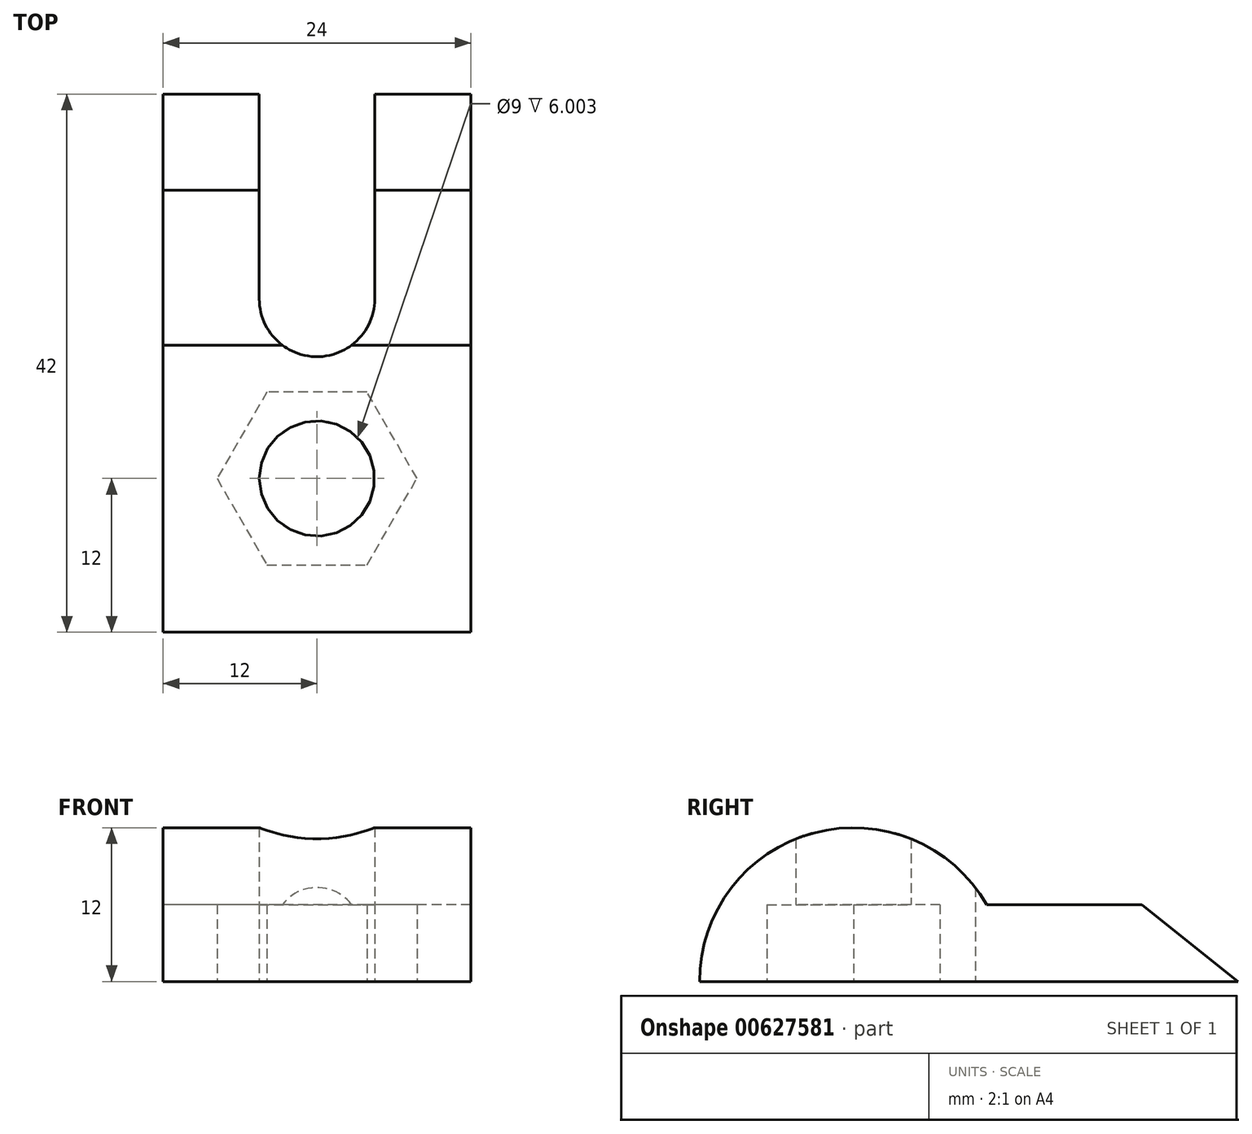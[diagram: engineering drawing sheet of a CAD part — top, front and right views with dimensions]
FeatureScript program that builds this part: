
annotation { "Feature Type Name" : "Feature", "Feature Type Description" : "" }
export const myFeature = defineFeature(function(context is Context, id is Id, definition is map)
    precondition{}
    {
        {
            var Q0;
            Q0=qCreatedBy(makeId("Right.planeOp"),FACE);
            var sketch = newSketch(context, id + "F0", { "sketchPlane" : qUnion([Q0])});
            skArc(sketch, "E0", {"start": v(10.4, 6) * mm, "mid": v(-3.1, 11.6) * mm, "end": v(-12, 0) * mm});
            skLineSegment(sketch, "E1", {"start": v(0, 0) * mm, "end": v(30, 0) * mm});
            skLineSegment(sketch, "E2", {"start": v(10.4, 6) * mm, "end": v(22.5, 6) * mm});
            skLineSegment(sketch, "E3", {"start": v(22.5, 6) * mm, "end": v(30, 0) * mm});
            skLineSegment(sketch, "E4", {"start": v(0, 0) * mm, "end": v(-12, 0) * mm});
            skSolve(sketch);
        }
        {
            var Q0;
            Q0=makeQuery(id+"F0.imprint","IMPRINT",FACE,{"disambiguationData":[TD([[makeQuery(id+"F0.imprint","IMPRINT",EDGE,{"derivedFrom":sQuery(id+"F0.wireOp",EDGE,"E0")}),1.0]])]});
            extrude(context, id + "F1", {"entities" : qUnion([Q0]), "depth" : 24 * mm, "offsetDistance" : 25 * mm});
        }
        {
            var Q0;
            Q0=makeQuery(id+"F1.opExtrude","SWEPT_FACE",FACE,{"disambiguationData":[OSD([sQuery(id+"F0.wireOp",EDGE,"E1"),sQuery(id+"F0.wireOp",EDGE,"E4")])]});
            var sketch = newSketch(context, id + "F2", { "sketchPlane" : qUnion([Q0])});
            skLineSegment(sketch, "E5", {"start": v(24, -30) * mm, "end": v(16.5, -30) * mm});
            skLineSegment(sketch, "E6", {"start": v(16.5, -30) * mm, "end": v(7.5, -30) * mm});
            skLineSegment(sketch, "E7", {"start": v(7.5, -30) * mm, "end": v(0, -30) * mm});
            skLineSegment(sketch, "E8", {"start": v(7.5, -30) * mm, "end": v(7.5, -14) * mm});
            skLineSegment(sketch, "E9", {"start": v(16.5, -30) * mm, "end": v(16.5, -14) * mm});
            skLineSegment(sketch, "E10", {"start": v(16.5, -14) * mm, "end": v(12, -14) * mm});
            skArc(sketch, "E11", {"start": v(16.5, -14) * mm, "mid": v(12, -9.5) * mm, "end": v(7.5, -14) * mm});
            skLineSegment(sketch, "E12", {"start": v(0, 0) * mm, "end": v(12, 0) * mm});
            skCircle(sketch, "E13", {"center": v(12, 0) * mm, "radius": 4.5 * mm});
            skLineSegment(sketch, "E14", {"start": v(12, 0) * mm, "end": v(12, -6.75) * mm});
            skCircle(sketch, "E15.cCircle", {"center": v(12, 0) * mm, "radius": 6.75 * mm, "construction": true});
            skLineSegment(sketch, "E15.0", {"start": v(15.9, -6.75) * mm, "end": v(8.1, -6.75) * mm});
            skLineSegment(sketch, "E15.1", {"start": v(8.1, -6.75) * mm, "end": v(4.2, 0) * mm});
            skLineSegment(sketch, "E15.2", {"start": v(4.2, 0) * mm, "end": v(8.1, 6.75) * mm});
            skLineSegment(sketch, "E15.3", {"start": v(8.1, 6.75) * mm, "end": v(15.9, 6.75) * mm});
            skLineSegment(sketch, "E15.4", {"start": v(15.9, 6.75) * mm, "end": v(19.8, 0) * mm});
            skLineSegment(sketch, "E15.5", {"start": v(19.8, 0) * mm, "end": v(15.9, -6.75) * mm});
            skPoint(sketch, "E15.0.midPoint", {"position": v(12, -6.75) * mm});
            skSolve(sketch);
        }
        {
            var Q0;
            Q0=makeQuery(id+"F2.imprint","IMPRINT",FACE,{"disambiguationData":[TD([[makeQuery(id+"F2.imprint","IMPRINT",EDGE,{"derivedFrom":sQuery(id+"F2.wireOp",EDGE,"E6")}),-1.0]])]});
            var Q1;
            Q1=makeQuery(id+"F2.imprint","IMPRINT",FACE,{"disambiguationData":[TD([[makeQuery(id+"F2.imprint","IMPRINT",EDGE,{"derivedFrom":sQuery(id+"F2.wireOp",EDGE,"E13")}),1.0]])]});
            extrude(context, id + "F3", {"entities" : qUnion([Q0, Q1]), "operationType" : NewBodyOperationType.REMOVE, "oppositeDirection" : true, "depth" : 25 * mm, "offsetDistance" : 25 * mm});
        }
        {
            var Q0;
            {var subQ8=sQuery(id+"F2.wireOp",EDGE,"E15.2");Q0=makeQuery(id+"F2.imprint","IMPRINT",FACE,{"disambiguationData":[TD([[makeQuery(id+"F2.imprint","IMPRINT",EDGE,{"derivedFrom":subQ8}),-1.0]])]});}
            var Q1;
            {var subQ3=sQuery(id+"F2.wireOp",EDGE,"E15.1");Q1=makeQuery(id+"F2.imprint","IMPRINT",FACE,{"disambiguationData":[TD([[makeQuery(id+"F2.imprint","IMPRINT",EDGE,{"derivedFrom":subQ3}),-1.0]])]});}
            extrude(context, id + "F4", {"entities" : qUnion([Q0, Q1]), "operationType" : NewBodyOperationType.REMOVE, "oppositeDirection" : true, "depth" : 6 * mm, "offsetDistance" : 25 * mm});
        }
        {
            var Q0;
            Q0=makeQuery(id+"F1.opExtrude","CAP_FACE",FACE,{"disambiguationData":[OSD([sQuery(id+"F0.wireOp",EDGE,"E0"),sQuery(id+"F0.wireOp",EDGE,"E1"),sQuery(id+"F0.wireOp",EDGE,"E2"),sQuery(id+"F0.wireOp",EDGE,"E3"),sQuery(id+"F0.wireOp",EDGE,"E4")])],"isStart":false});
            var sketch = newSketch(context, id + "F5", { "sketchPlane" : qUnion([Q0])});
            skLineSegment(sketch, "E16", {"start": v(22.5, 6) * mm, "end": v(7.5, 6) * mm});
            skLineSegment(sketch, "E17.bottom", {"start": v(7.5, 6) * mm, "end": v(22.5, 6) * mm});
            skLineSegment(sketch, "E17.top", {"start": v(7.5, 11) * mm, "end": v(22.5, 11) * mm});
            skLineSegment(sketch, "E17.left", {"start": v(7.5, 6) * mm, "end": v(7.5, 11) * mm});
            skLineSegment(sketch, "E17.right", {"start": v(22.5, 6) * mm, "end": v(22.5, 11) * mm});
            skSolve(sketch);
        }
        {
            var Q0;
            {var subQ2=sQuery(id+"F5.wireOp",EDGE,"E17.top");Q0=makeQuery(id+"F5.imprint","IMPRINT",FACE,{"disambiguationData":[TD([[makeQuery(id+"F5.imprint","IMPRINT",EDGE,{"derivedFrom":subQ2}),-1.0]])]});}
            var Q1;
            {var subQ0=sQuery(id+"F5.wireOp",EDGE,"E17.bottom");var subQ1=makeQuery(id+"F1.opExtrude","CAP_EDGE",EDGE,{"disambiguationData":[OSD([sQuery(id+"F0.wireOp",EDGE,"E0")])],"isStart":false});var subQ2=makeQuery(id+"F5.imprint","INTERSECT",VERTEX,{"derivedFrom":[subQ1,subQ0]});Q1=makeQuery(id+"F5.imprint","IMPRINT",FACE,{"disambiguationData":[TD([[makeQuery(id+"F5.imprint","IMPRINT",EDGE,{"disambiguationData":[TD([[subQ2,1.0]])],"derivedFrom":subQ0}),1.0]])]});}
            extrude(context, id + "F6", {"entities" : qUnion([Q0, Q1]), "operationType" : NewBodyOperationType.REMOVE, "oppositeDirection" : true, "depth" : 25 * mm, "offsetDistance" : 25 * mm});
        }
    });
